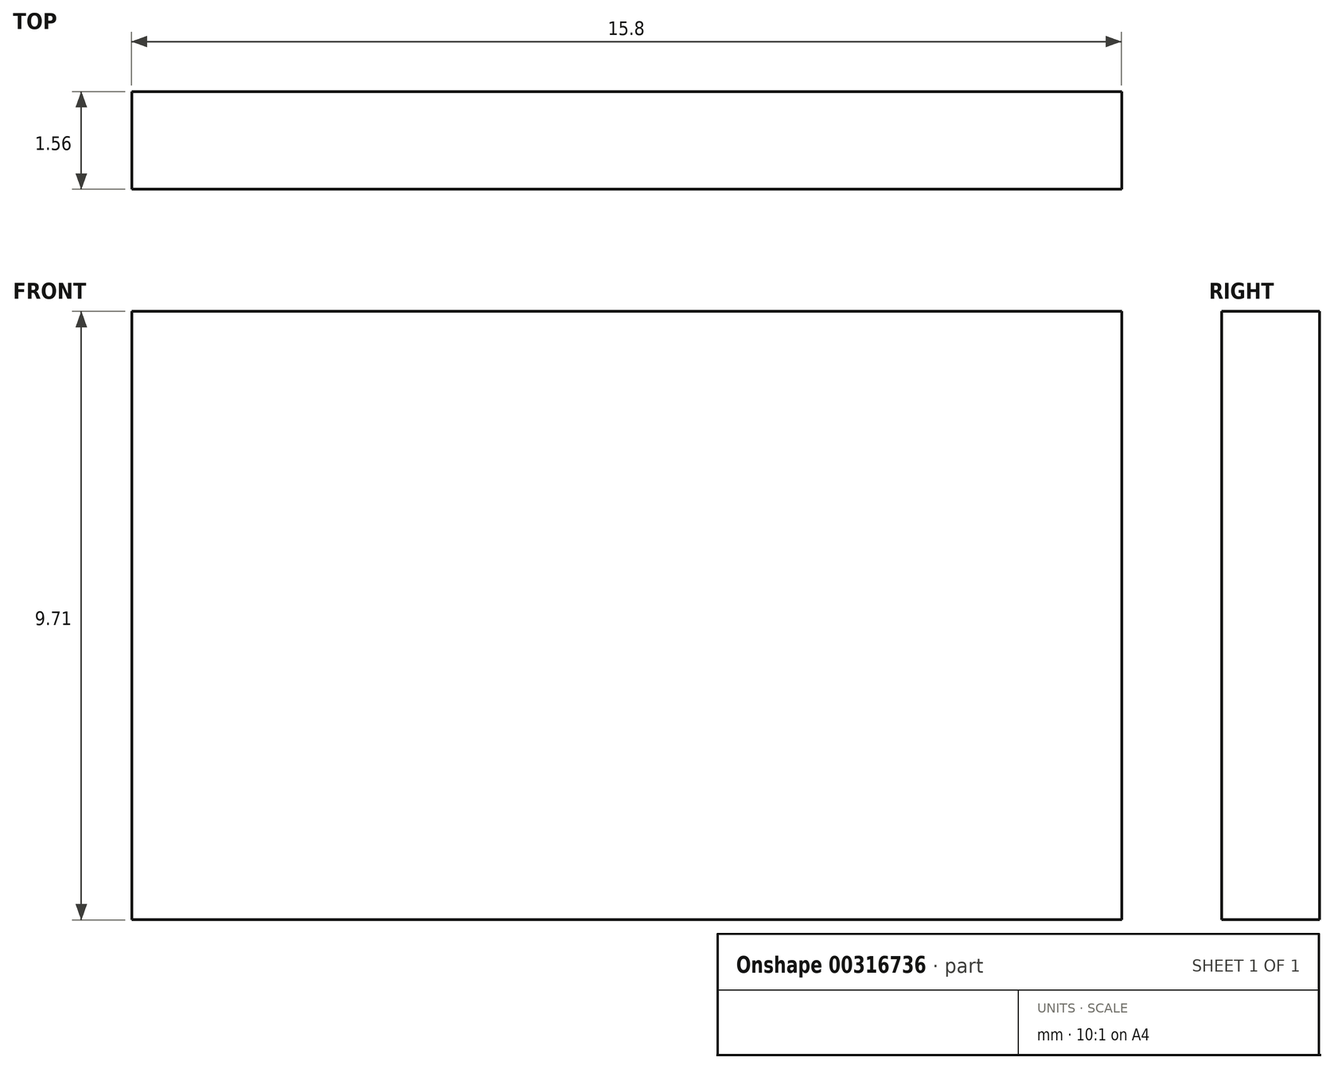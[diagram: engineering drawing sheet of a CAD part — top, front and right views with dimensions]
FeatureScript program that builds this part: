
annotation { "Feature Type Name" : "Feature", "Feature Type Description" : "" }
export const myFeature = defineFeature(function(context is Context, id is Id, definition is map)
    precondition{}
    {
        {
            var Q0;
            Q0=qCreatedBy(makeId("Front.planeOp"),FACE);
            var sketch = newSketch(context, id + "F0", { "sketchPlane" : qUnion([Q0])});
            skLineSegment(sketch, "E0", {"start": v(-56.16, 13.84) * mm, "end": v(-40.36, 13.84) * mm});
            skLineSegment(sketch, "E1", {"start": v(-56.16, 13.84) * mm, "end": v(-56.16, 4.13) * mm});
            skLineSegment(sketch, "E2", {"start": v(-56.16, 4.13) * mm, "end": v(-40.36, 4.13) * mm});
            skLineSegment(sketch, "E3", {"start": v(-40.36, 4.13) * mm, "end": v(-40.36, 13.84) * mm});
            skSolve(sketch);
        }
        {
            var Q0;
            Q0 = qSketchRegion(id + "F0", true);
            extrude(context, id + "F1", {"entities" : qUnion([Q0]), "depth" : 1.56 * mm});
        }
    });
